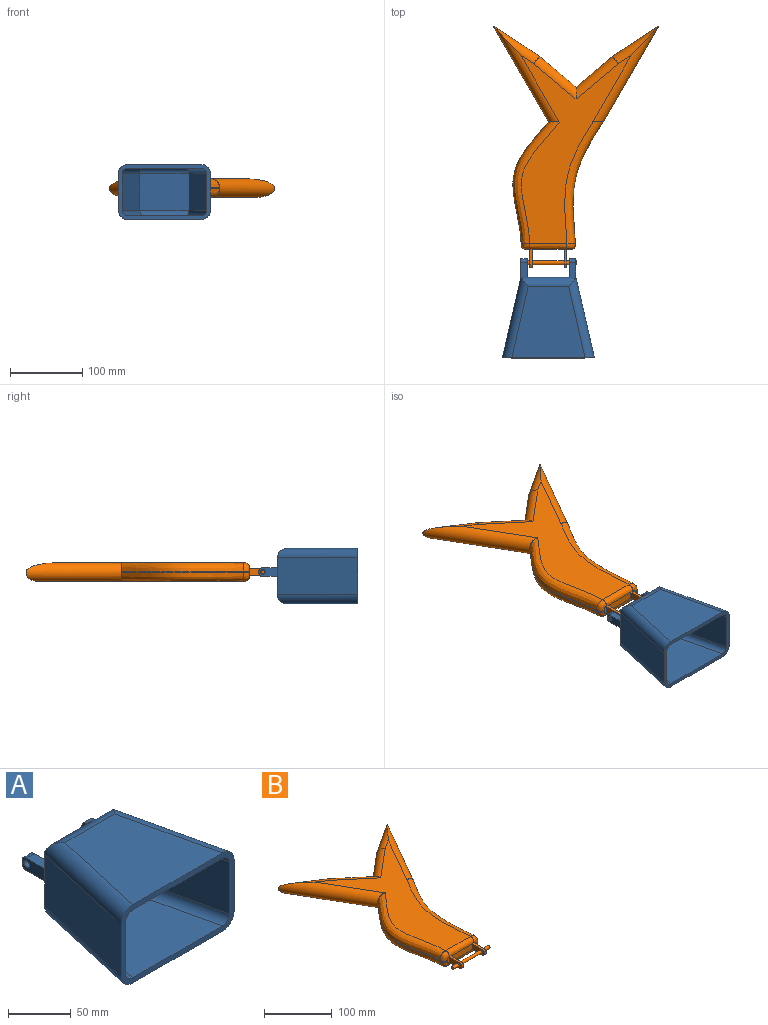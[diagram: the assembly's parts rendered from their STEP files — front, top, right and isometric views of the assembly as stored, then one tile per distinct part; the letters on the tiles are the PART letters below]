
ASSEMBLY  parts=2 mates=1
PART A: 41 faces, bbox 127x139.7x76.2 mm
  f0: plane 76.2x50.8mm, normal (0,1,0), area 3658.6mm2, adj f1,f3,f7,f10,f23,f25,f26,f29
  f1: plane 111.44x50.8mm, normal (-0.97,0.22,0), area 5806.4mm2, adj f0,f2,f8,f11,f28
  f2: plane 127x76.2mm, normal (0,-1,0), area 1887.6mm2, adj f1,f3,f4,f5,f6,f8,f9,f11
  f3: plane 111.44x50.8mm, normal (0.97,0.22,0), area 5806.4mm2, adj f0,f2,f6,f9,f24
  f4: plane 100.95x98.74mm, normal (0,0,1), area 7745.6mm2, adj f2,f9,f10,f11
  f5: plane 100.95x98.74mm, normal (0,0,-1), area 7745.6mm2, adj f2,f6,f7,f8
  f6: cylinder r=12.7mm len=114.26mm, axis (-0.22,0.97,0), area 2185.8mm2, adj f2,f3,f5,f7
  f7: cylinder r=12.7mm len=76.2mm, axis (-1,0,0), area 1373.2mm2, adj f0,f5,f6,f8
  f8: cylinder r=12.7mm len=114.26mm, axis (-0.22,-0.97,0), area 2185.8mm2, adj f1,f2,f5,f7
  f9: cylinder r=12.7mm len=114.26mm, axis (0.22,-0.97,0), area 2185.8mm2, adj f2,f3,f4,f10
  f10: cylinder r=12.7mm len=76.2mm, axis (1,0,0), area 1373.2mm2, adj f0,f4,f9,f11
  f11: cylinder r=12.7mm len=114.26mm, axis (0.22,0.97,0), area 2185.8mm2, adj f1,f2,f4,f10
  f12: plane 68.1x50.8mm, normal (0,-1,0), area 3459.2mm2, adj f13,f14,f18,f21
  f13: plane 106.36x50.8mm, normal (0.97,-0.22,0), area 5541.8mm2, adj f2,f12,f19,f22
  f14: plane 106.36x50.8mm, normal (-0.97,-0.22,0), area 5541.8mm2, adj f2,f12,f17,f20
  f15: plane 100.95x98.74mm, normal (0,0,-1), area 7745.6mm2, adj f2,f20,f21,f22
  f16: plane 100.95x98.74mm, normal (0,0,1), area 7745.6mm2, adj f2,f17,f18,f19
  f17: cylinder r=7.62mm len=108.06mm, axis (-0.22,0.97,0), area 1271.8mm2, adj f2,f14,f16,f18
  f18: cylinder r=7.62mm len=68.1mm, axis (-1,0,0), area 762.2mm2, adj f12,f16,f17,f19
  f19: cylinder r=7.62mm len=108.06mm, axis (-0.22,-0.97,0), area 1271.8mm2, adj f2,f13,f16,f18
  f20: cylinder r=7.62mm len=108.06mm, axis (0.22,-0.97,0), area 1271.8mm2, adj f2,f14,f15,f21
  f21: cylinder r=7.62mm len=68.1mm, axis (1,0,0), area 762.2mm2, adj f12,f15,f20,f22
  f22: cylinder r=7.62mm len=108.06mm, axis (0.22,0.97,0), area 1271.8mm2, adj f2,f13,f15,f21
  f23: plane 20.32x8.87mm, normal (0,0,1), area 180.2mm2, adj f0,f24,f26,f36
  f24: plane 25.4x11.97mm, normal (1,0,0), area 263.8mm2, adj f3,f23,f25,f27,f35,f36,f39
  f25: plane 20.32x8.87mm, normal (0,0,-1), area 180.2mm2, adj f0,f24,f26,f35
  f26: plane 25.4x11.97mm, normal (-1,0,0), area 263.8mm2, adj f0,f23,f25,f27,f35,f36,f39
  f27: plane 8.87x1.81mm, normal (0,1,0), area 16.1mm2, adj f24,f26,f35,f36
  f28: plane 25.4x11.97mm, normal (-1,0,0), area 263.8mm2, adj f1,f29,f31,f32,f33,f34,f40
  f29: plane 20.32x8.87mm, normal (0,0,1), area 180.2mm2, adj f0,f28,f30,f34
  f30: plane 25.4x11.97mm, normal (1,0,0), area 262.9mm2, adj f0,f29,f31,f32,f33,f34,f38,f40
  f31: plane 20.32x8.87mm, normal (0,0,-1), area 180.2mm2, adj f0,f28,f30,f33
  f32: plane 8.87x1.81mm, normal (0,1,0), area 16.1mm2, adj f28,f30,f33,f34
  f33: bspline ~9.76x5.08mm, area 73.1mm2, adj f28,f30,f31,f32
  f34: bspline ~9.76x5.08mm, area 73.1mm2, adj f28,f29,f30,f32
  f35: bspline ~9.76x5.08mm, area 73.1mm2, adj f24,f25,f26,f27
  f36: bspline ~9.76x5.08mm, area 73.1mm2, adj f23,f24,f26,f27
  f37: plane 5.49x5.45mm, normal (1,0,0), area 0.9mm2, adj f38,f40
  f38: cylinder r=3.17mm len=5.49mm, axis (-1,0,0), area 15.4mm2, adj f30,f37,f40
  f39: cylinder r=3.17mm len=8.87mm, axis (-1,0,0), area 176.9mm2, adj f24,f26
  f40: cylinder r=3.17mm len=8.87mm, axis (-1,0,0), area 162mm2, adj f28,f30,f37,f38
PART B: 54 faces, bbox 242.9x340.8x25.8 mm
  f0: plane 44.01x10.16mm, normal (0,-1,0), area 447.2mm2, adj f30,f35,f37,f43
  f1: plane 10.52x4.42mm, normal (0,-1,0), area 38mm2, adj f32,f34,f36,f39
  f2: plane 13.93x11.29mm, normal (0,1,0), area 11.8mm2, adj f17,f28
  f3: plane 13.93x11.29mm, normal (0,1,0), area 11.8mm2, adj f17,f26
  f4: plane 11.35x1.71mm, normal (0,-1,0), area 5.1mm2, adj f12,f23,f25,f27
  f5: plane 50.59x42.45mm, normal (-0.64,0.77,0), area 838.7mm2, adj f6,f9,f11,f15
  f6: plane 50.59x42.45mm, normal (0.64,0.77,0), area 838.7mm2, adj f5,f7,f11,f14
  f7: plane 63.71x41.8mm, normal (0.55,0.84,0), area 890.8mm2, adj f6,f11,f12,f13
  f8: plane 2.92x0.1mm, normal (0,-1,0), area 0.2mm2, adj f17,f21,f26,f28
  f9: plane 63.71x41.8mm, normal (-0.55,0.84,0), area 890.8mm2, adj f5,f11,f16,f17
  f10: plane 262.1x153.15mm, normal (0,0,1), area 14249.8mm2, adj f12,f13,f14,f15,f16,f17,f22,f27
  f11: plane 286.37x181.38mm, normal (0,0,-1), area 16960.9mm2, adj f5,f6,f7,f9,f12,f17,f20,f25
  f12: cylinder r=12.7mm len=145.61mm, axis (0.5,-0.87,0), area 5617.9mm2, adj f4,f7,f10,f11,f13,f18,f19,f25
  f13: cylinder r=12.7mm len=70.68mm, axis (0.84,-0.55,0), area 1125.2mm2, adj f7,f10,f12,f14
  f14: cylinder r=12.7mm len=66.92mm, axis (0.77,-0.64,0), area 1416.3mm2, adj f6,f10,f13,f15
  f15: cylinder r=12.7mm len=66.92mm, axis (0.77,0.64,0), area 1416.3mm2, adj f5,f10,f14,f16
  f16: cylinder r=12.7mm len=70.68mm, axis (0.84,0.55,0), area 1125.2mm2, adj f9,f10,f15,f17
  f17: cylinder r=12.7mm len=144.62mm, axis (-0.5,-0.87,0), area 5613.7mm2, adj f2,f3,f8,f9,f10,f11,f16,f20
  f18: plane 9.46x6.32mm, normal (0,1,0), area 2.8mm2, adj f12,f27
  f19: plane 9.46x6.32mm, normal (0,1,0), area 2.8mm2, adj f12,f25
  f20: plane 0.65x0.01mm, normal (0,1,0), area 0mm2, adj f11,f17
  f21: extruded ~168.34x42.18mm, area 362.1mm2, adj f8,f26,f28,f31
  f22: plane 0.65x0.01mm, normal (0,1,0), area 0mm2, adj f10,f17
  f23: extruded ~169.08x49.79mm, area 377.4mm2, adj f4,f25,f27,f34
  f24: plane 10.52x4.45mm, normal (0,-1,0), area 38.1mm2, adj f29,f31,f33,f41
  f25: bspline ~197.34x78.42mm, area 3532mm2, adj f4,f11,f12,f19,f23,f36
  f26: bspline ~202.21x59.39mm, area 3380.6mm2, adj f3,f8,f11,f17,f21,f33
  f27: bspline ~233.85x108.2mm, area 3529.3mm2, adj f4,f10,f12,f18,f23,f32
  f28: bspline ~202.21x59.35mm, area 3380.7mm2, adj f2,f8,f10,f17,f21,f29
  f29: bspline ~12.5x11.71mm, area 196.1mm2, adj f24,f28,f30,f31
  f30: bspline ~51.63x7.62mm, area 638.7mm2, adj f0,f10,f29,f32,f38,f42
  f31: bspline ~8.59x8.38mm, area 27mm2, adj f21,f24,f29,f33
  f32: bspline ~11.7x11.68mm, area 184.6mm2, adj f1,f27,f30,f34
  f33: bspline ~12.5x11.71mm, area 195.9mm2, adj f24,f26,f31,f35
  f34: bspline ~7.63x7.63mm, area 25.2mm2, adj f1,f23,f32,f36
  f35: bspline ~51.64x7.62mm, area 638.7mm2, adj f0,f11,f33,f36,f40,f44
  f36: bspline ~11.68x11.68mm, area 184.6mm2, adj f1,f25,f34,f35
  f37: plane 25.4x10.16mm, normal (1,0,0), area 229.2mm2, adj f0,f38,f40,f45,f52,f53
  f38: plane 20.32x3.81mm, normal (0,0,1), area 77.4mm2, adj f30,f37,f39,f53
  f39: plane 25.4x10.16mm, normal (-1,0,0), area 229.2mm2, adj f1,f38,f40,f48,f52,f53
  f40: plane 20.32x3.81mm, normal (0,0,-1), area 77.4mm2, adj f35,f37,f39,f52
  f41: plane 25.4x10.16mm, normal (1,0,0), area 229.2mm2, adj f24,f42,f44,f47,f50,f51
  f42: plane 20.32x3.81mm, normal (0,0,1), area 77.4mm2, adj f30,f41,f43,f51
  f43: plane 25.4x10.16mm, normal (-1,0,0), area 229.2mm2, adj f0,f42,f44,f45,f50,f51
  f44: plane 20.32x3.81mm, normal (0,0,-1), area 77.4mm2, adj f35,f41,f43,f50
  f45: cylinder r=2.54mm len=44.01mm, axis (1,0,0), area 702.4mm2, adj f37,f43
  f46: plane 5.08x5.08mm, normal (1,0,0), area 20.3mm2, adj f47
  f47: cylinder r=2.54mm len=12.52mm, axis (1,0,0), area 199.8mm2, adj f41,f46
  f48: cylinder r=2.54mm len=12.05mm, axis (1,0,0), area 192.3mm2, adj f39,f49
  f49: plane 5.08x5.08mm, normal (-1,0,0), area 20.3mm2, adj f48
  f50: bspline ~5.08x5.08mm, area 31.4mm2, adj f41,f43,f44,f51
  f51: bspline ~5.08x5.08mm, area 31.4mm2, adj f41,f42,f43,f50
  f52: bspline ~5.08x5.08mm, area 31.4mm2, adj f37,f39,f40,f53
  f53: bspline ~5.08x5.08mm, area 31.4mm2, adj f37,f38,f39,f52
PLACE A t=(37.59,42.41,-105.92)mm
PLACE B t=(106.44,350,-75.09)mm
MATE cylindrical B.f45 <-> A.f38  axis (1,0,0) through (106.44,107,-62.09)mm
